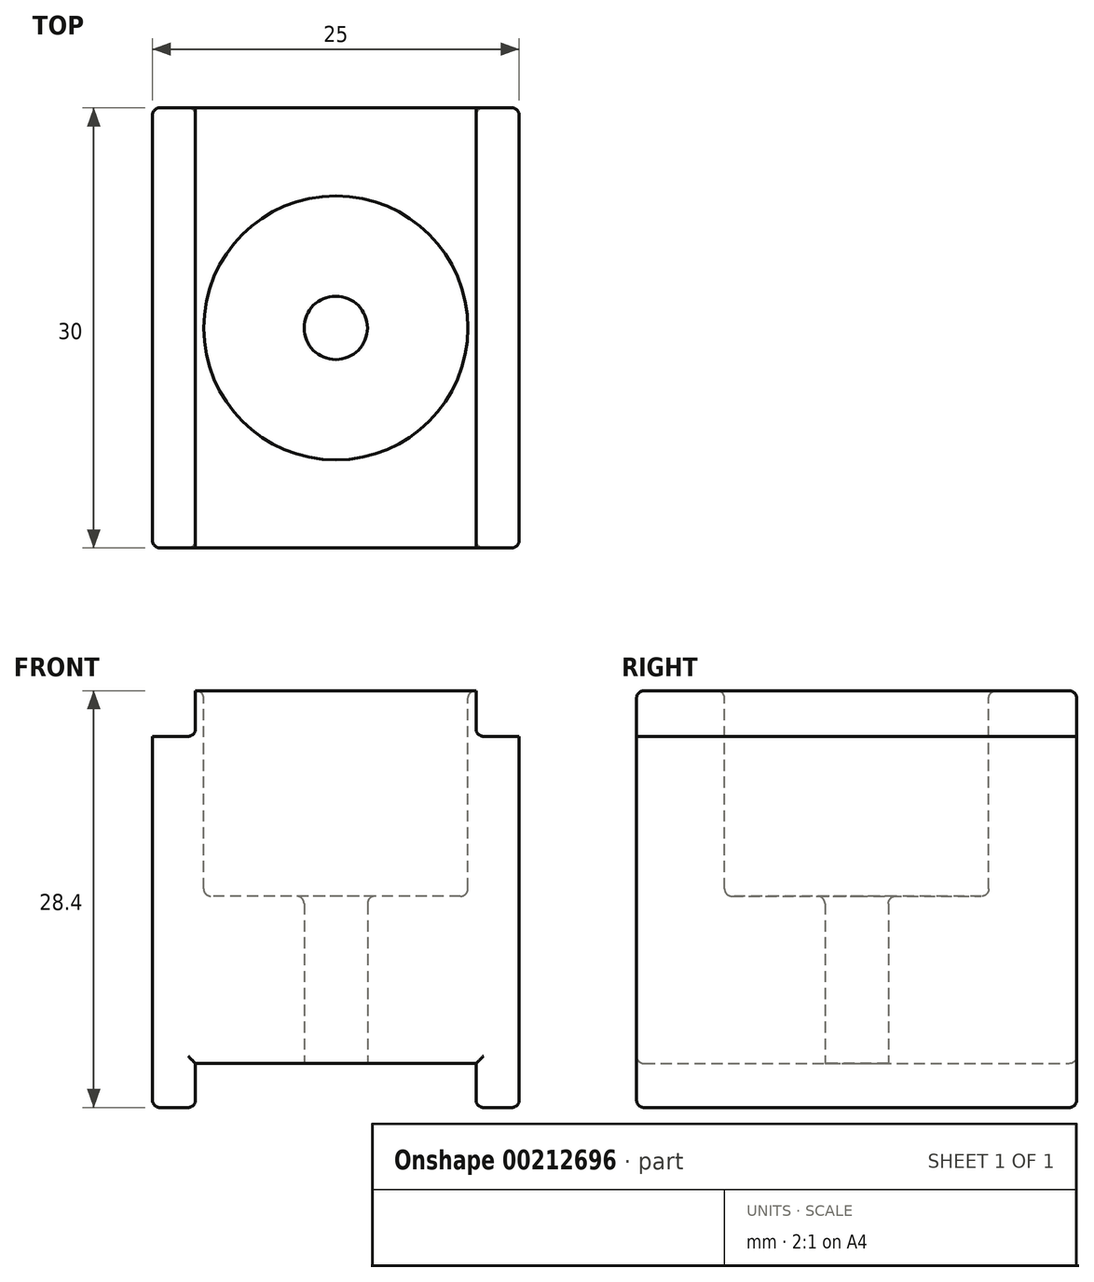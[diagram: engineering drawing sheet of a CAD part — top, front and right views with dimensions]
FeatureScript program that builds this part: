
annotation { "Feature Type Name" : "Feature", "Feature Type Description" : "" }
export const myFeature = defineFeature(function(context is Context, id is Id, definition is map)
    precondition{}
    {
        {
            var Q0;
            Q0=qCreatedBy(makeId("Top.planeOp"),FACE);
            var sketch = newSketch(context, id + "F0", { "sketchPlane" : qUnion([Q0])});
            skLineSegment(sketch, "E0.bottom", {"start": v(12.5, 15) * mm, "end": v(-12.5, 15) * mm});
            skLineSegment(sketch, "E0.top", {"start": v(12.5, -15) * mm, "end": v(-12.5, -15) * mm});
            skLineSegment(sketch, "E0.left", {"start": v(12.5, 15) * mm, "end": v(12.5, -15) * mm});
            skLineSegment(sketch, "E0.right", {"start": v(-12.5, 15) * mm, "end": v(-12.5, -15) * mm});
            skPoint(sketch, "E0.middle", {"position": v(0, 0) * mm});
            skPoint(sketch, "E1.end.orphan", {"position": v(-9.56, -15) * mm});
            skPoint(sketch, "E1.start.orphan", {"position": v(-9.56, 15) * mm});
            skPoint(sketch, "E2.MirrorCS.end.orphan", {"position": v(9.56, -15) * mm});
            skPoint(sketch, "E2.MirrorCS.start.orphan", {"position": v(9.56, 15) * mm});
            skSolve(sketch);
        }
        {
            var Q0;
            Q0=makeQuery(id+"F0.imprint","IMPRINT",FACE,{"disambiguationData":[TD([[makeQuery(id+"F0.imprint","IMPRINT",EDGE,{"derivedFrom":sQuery(id+"F0.wireOp",EDGE,"E0.bottom")}),1.0]])]});
            extrude(context, id + "F1", {"entities" : qUnion([Q0]), "endBound" : BoundingType.SYMMETRIC, "depth" : 25.4 * mm});
        }
        {
            var Q0;
            Q0=makeQuery(id+"F1.opExtrude","CAP_FACE",FACE,{"disambiguationData":[OSD([sQuery(id+"F0.wireOp",EDGE,"E0.bottom"),sQuery(id+"F0.wireOp",EDGE,"E0.top"),sQuery(id+"F0.wireOp",EDGE,"E0.left"),sQuery(id+"F0.wireOp",EDGE,"E0.right")])],"isStart":true});
            var sketch = newSketch(context, id + "F2", { "sketchPlane" : qUnion([Q0])});
            skLineSegment(sketch, "E3", {"start": v(-9.56, 15) * mm, "end": v(-9.56, -15) * mm});
            skLineSegment(sketch, "E4.MirrorCS", {"start": v(9.56, 15) * mm, "end": v(9.56, -15) * mm});
            skSolve(sketch);
        }
        {
            var Q0;
            {var subQ0=sQuery(id+"F2.wireOp",EDGE,"E3");Q0=makeQuery(id+"F2.imprint","IMPRINT",FACE,{"disambiguationData":[TD([[makeQuery(id+"F2.imprint","IMPRINT",EDGE,{"derivedFrom":subQ0}),-1.0]])]});}
            var Q1;
            {var subQ0=sQuery(id+"F2.wireOp",EDGE,"E4.MirrorCS");Q1=makeQuery(id+"F2.imprint","IMPRINT",FACE,{"disambiguationData":[TD([[makeQuery(id+"F2.imprint","IMPRINT",EDGE,{"derivedFrom":subQ0}),1.0]])]});}
            extrude(context, id + "F3", {"entities" : qUnion([Q0, Q1]), "operationType" : NewBodyOperationType.ADD, "depth" : 3 * mm});
        }
        {
            var Q0;
            Q0=makeQuery(id+"F1.opExtrude","CAP_FACE",FACE,{"disambiguationData":[OSD([sQuery(id+"F0.wireOp",EDGE,"E0.bottom"),sQuery(id+"F0.wireOp",EDGE,"E0.top"),sQuery(id+"F0.wireOp",EDGE,"E0.left"),sQuery(id+"F0.wireOp",EDGE,"E0.right")])],"isStart":false});
            var sketch = newSketch(context, id + "F4", { "sketchPlane" : qUnion([Q0])});
            skCircle(sketch, "E5", {"center": v(0, 0) * mm, "radius": 9 * mm});
            skLineSegment(sketch, "E6", {"start": v(-9.56, 15) * mm, "end": v(-9.56, -15) * mm});
            skLineSegment(sketch, "E7.MirrorCS", {"start": v(9.56, 15) * mm, "end": v(9.56, -15) * mm});
            skSolve(sketch);
        }
        {
            var Q0;
            Q0=makeQuery(id+"F4.imprint","IMPRINT",FACE,{"disambiguationData":[TD([[makeQuery(id+"F4.imprint","IMPRINT",EDGE,{"derivedFrom":sQuery(id+"F4.wireOp",EDGE,"E5")}),1.0]])]});
            extrude(context, id + "F5", {"entities" : qUnion([Q0]), "operationType" : NewBodyOperationType.REMOVE, "oppositeDirection" : true, "depth" : 14 * mm});
        }
        {
            var Q0;
            {var subQ0=sQuery(id+"F4.wireOp",EDGE,"E7.MirrorCS");Q0=makeQuery(id+"F4.imprint","IMPRINT",FACE,{"disambiguationData":[TD([[makeQuery(id+"F4.imprint","IMPRINT",EDGE,{"derivedFrom":subQ0}),1.0]])]});}
            var Q1;
            {var subQ0=sQuery(id+"F4.wireOp",EDGE,"E6");Q1=makeQuery(id+"F4.imprint","IMPRINT",FACE,{"disambiguationData":[TD([[makeQuery(id+"F4.imprint","IMPRINT",EDGE,{"derivedFrom":subQ0}),-1.0]])]});}
            extrude(context, id + "F6", {"entities" : qUnion([Q0, Q1]), "operationType" : NewBodyOperationType.REMOVE, "oppositeDirection" : true, "depth" : 3.1 * mm});
        }
        {
            var Q0;
            Q0=makeQuery(id+"F1.opExtrude","CAP_FACE",FACE,{"disambiguationData":[OSD([sQuery(id+"F0.wireOp",EDGE,"E0.bottom"),sQuery(id+"F0.wireOp",EDGE,"E0.top"),sQuery(id+"F0.wireOp",EDGE,"E0.left"),sQuery(id+"F0.wireOp",EDGE,"E0.right")])],"isStart":true});
            var sketch = newSketch(context, id + "F7", { "sketchPlane" : qUnion([Q0])});
            skCircle(sketch, "E8", {"center": v(0, 0) * mm, "radius": 2.16 * mm});
            skSolve(sketch);
        }
        {
            var Q0;
            Q0=makeQuery(id+"F7.imprint","IMPRINT",FACE,{"disambiguationData":[TD([[makeQuery(id+"F7.imprint","IMPRINT",EDGE,{"derivedFrom":sQuery(id+"F7.wireOp",EDGE,"E8")}),1.0]])]});
            extrude(context, id + "F8", {"entities" : qUnion([Q0]), "operationType" : NewBodyOperationType.REMOVE, "endBound" : BoundingType.THROUGH_ALL, "oppositeDirection" : true, "depth" : 25 * mm});
        }
        {
            var Q0;
            Q0=makeQuery(id+"F3.opExtrude","CAP_EDGE",EDGE,{"disambiguationData":[OSD([sQuery(id+"F0.wireOp",EDGE,"E0.right")])],"isStart":false});
            var Q1;
            Q1=makeQuery(id+"F3.opExtrude","CAP_EDGE",EDGE,{"disambiguationData":[OSD([sQuery(id+"F2.wireOp",EDGE,"E3")])],"isStart":false});
            var Q2;
            Q2=makeQuery(id+"F3.opExtrude","CAP_EDGE",EDGE,{"disambiguationData":[OSD([sQuery(id+"F2.wireOp",EDGE,"E4.MirrorCS")])],"isStart":false});
            var Q3;
            Q3=makeQuery(id+"F3.opExtrude","CAP_EDGE",EDGE,{"disambiguationData":[OSD([sQuery(id+"F0.wireOp",EDGE,"E0.left")])],"isStart":false});
            var Q4;
            Q4=makeQuery(id+"F1.opExtrude","CAP_EDGE",EDGE,{"disambiguationData":[OSD([sQuery(id+"F0.wireOp",EDGE,"E0.bottom")])],"isStart":true});
            var Q5;
            Q5=makeQuery(id+"F1.opExtrude","CAP_EDGE",EDGE,{"disambiguationData":[OSD([sQuery(id+"F0.wireOp",EDGE,"E0.top")])],"isStart":true});
            var Q6;
            {var subQ0=sQuery(id+"F0.wireOp",EDGE,"E0.left");var subQ1=sQuery(id+"F0.wireOp",EDGE,"E0.bottom");Q6=makeQuery(id+"F3.boolean.opBoolean","MERGE",EDGE,{"derivedFrom":[makeQuery(id+"F1.opExtrude","SWEPT_EDGE",EDGE,{"disambiguationData":[OSD([subQ1,subQ0])]}),makeQuery(id+"F3.opExtrude","SWEPT_EDGE",EDGE,{"disambiguationData":[OSD([subQ1,subQ0])]})]});}
            var Q7;
            {var subQ0=sQuery(id+"F0.wireOp",EDGE,"E0.left");var subQ1=sQuery(id+"F0.wireOp",EDGE,"E0.top");Q7=makeQuery(id+"F3.boolean.opBoolean","MERGE",EDGE,{"derivedFrom":[makeQuery(id+"F1.opExtrude","SWEPT_EDGE",EDGE,{"disambiguationData":[OSD([subQ1,subQ0])]}),makeQuery(id+"F3.opExtrude","SWEPT_EDGE",EDGE,{"disambiguationData":[OSD([subQ1,subQ0])]})]});}
            var Q8;
            {var subQ0=sQuery(id+"F0.wireOp",EDGE,"E0.right");var subQ1=sQuery(id+"F0.wireOp",EDGE,"E0.bottom");Q8=makeQuery(id+"F3.boolean.opBoolean","MERGE",EDGE,{"derivedFrom":[makeQuery(id+"F1.opExtrude","SWEPT_EDGE",EDGE,{"disambiguationData":[OSD([subQ1,subQ0])]}),makeQuery(id+"F3.opExtrude","SWEPT_EDGE",EDGE,{"disambiguationData":[OSD([subQ1,subQ0])]})]});}
            var Q9;
            Q9=makeQuery(id+"F1.opExtrude","CAP_EDGE",EDGE,{"disambiguationData":[OSD([sQuery(id+"F0.wireOp",EDGE,"E0.bottom")])],"isStart":false});
            var Q10;
            Q10=makeQuery(id+"F6.boolean.opBoolean","COPY",EDGE,{"derivedFrom":makeQuery(id+"F6.opExtrude","CAP_EDGE",EDGE,{"disambiguationData":[OSD([sQuery(id+"F0.wireOp",EDGE,"E0.left")])],"isStart":false})});
            var Q11;
            Q11=makeQuery(id+"F6.boolean.opBoolean","COPY",EDGE,{"derivedFrom":makeQuery(id+"F6.opExtrude","CAP_EDGE",EDGE,{"disambiguationData":[OSD([sQuery(id+"F4.wireOp",EDGE,"E7.MirrorCS")])],"isStart":true})});
            var Q12;
            Q12=makeQuery(id+"F6.boolean.opBoolean","COPY",EDGE,{"derivedFrom":makeQuery(id+"F6.opExtrude","CAP_EDGE",EDGE,{"disambiguationData":[OSD([sQuery(id+"F4.wireOp",EDGE,"E6")])],"isStart":true})});
            var Q13;
            Q13=makeQuery(id+"F6.boolean.opBoolean","COPY",EDGE,{"derivedFrom":makeQuery(id+"F6.opExtrude","CAP_EDGE",EDGE,{"disambiguationData":[OSD([sQuery(id+"F0.wireOp",EDGE,"E0.right")])],"isStart":false})});
            var Q14;
            Q14=makeQuery(id+"F1.opExtrude","CAP_EDGE",EDGE,{"disambiguationData":[OSD([sQuery(id+"F0.wireOp",EDGE,"E0.top")])],"isStart":false});
            var Q15;
            Q15=makeQuery(id+"F6.boolean.opBoolean","COPY",EDGE,{"derivedFrom":makeQuery(id+"F6.opExtrude","CAP_EDGE",EDGE,{"disambiguationData":[OSD([sQuery(id+"F4.wireOp",EDGE,"E7.MirrorCS")])],"isStart":false})});
            var Q16;
            Q16=makeQuery(id+"F6.boolean.opBoolean","COPY",EDGE,{"derivedFrom":makeQuery(id+"F6.opExtrude","CAP_EDGE",EDGE,{"disambiguationData":[OSD([sQuery(id+"F4.wireOp",EDGE,"E6")])],"isStart":false})});
            var Q17;
            Q17=makeQuery(id+"F3.opExtrude","CAP_EDGE",EDGE,{"disambiguationData":[OSD([sQuery(id+"F2.wireOp",EDGE,"E4.MirrorCS")])],"isStart":true});
            var Q18;
            Q18=makeQuery(id+"F3.opExtrude","CAP_EDGE",EDGE,{"disambiguationData":[OSD([sQuery(id+"F2.wireOp",EDGE,"E3")])],"isStart":true});
            fillet(context, id + "F9", {"entities" : qUnion([Q0, Q1, Q2, Q3, Q4, Q5, Q6, Q7, Q8, Q9, Q10, Q11, Q12, Q13, Q14, Q15, Q16, Q17, Q18]), "radius" : .5 * mm, "tangentPropagation" : true, "allowEdgeOverflow" : false});
        }
        {
            var Q0;
            Q0=makeQuery(id+"F6.boolean.opBoolean","COPY",EDGE,{"derivedFrom":makeQuery(id+"F6.opExtrude","SWEPT_EDGE",EDGE,{"disambiguationData":[OSD([sQuery(id+"F0.wireOp",EDGE,"E0.bottom"),sQuery(id+"F4.wireOp",EDGE,"E6")])]})});
            var Q1;
            Q1=makeQuery(id+"F6.boolean.opBoolean","COPY",EDGE,{"derivedFrom":makeQuery(id+"F6.opExtrude","SWEPT_EDGE",EDGE,{"disambiguationData":[OSD([sQuery(id+"F0.wireOp",EDGE,"E0.bottom"),sQuery(id+"F4.wireOp",EDGE,"E7.MirrorCS")])]})});
            var Q2;
            {var subQ0=sQuery(id+"F0.wireOp",EDGE,"E0.bottom");var subQ1=makeQuery(id+"F1.opExtrude","CAP_EDGE",EDGE,{"disambiguationData":[OSD([subQ0])],"isStart":true});Q2=makeQuery(id+"F3.opExtrude","CAP_EDGE",EDGE,{"disambiguationData":[OSD([subQ0]),TDD([makeQuery(id+"F2.imprint","IMPRINT",EDGE,{"disambiguationData":[TD([[makeQuery(id+"F2.imprint","INTERSECT",VERTEX,{"derivedFrom":[subQ1,makeQuery(id+"F1.opExtrude","CAP_EDGE",EDGE,{"disambiguationData":[OSD([sQuery(id+"F0.wireOp",EDGE,"E0.left")])],"isStart":true})]}),-1.0]])],"derivedFrom":subQ1})])],"isStart":false});}
            var Q3;
            {var subQ0=sQuery(id+"F0.wireOp",EDGE,"E0.bottom");var subQ1=makeQuery(id+"F1.opExtrude","CAP_EDGE",EDGE,{"disambiguationData":[OSD([subQ0])],"isStart":true});Q3=makeQuery(id+"F3.opExtrude","CAP_EDGE",EDGE,{"disambiguationData":[OSD([subQ0]),TDD([makeQuery(id+"F2.imprint","IMPRINT",EDGE,{"disambiguationData":[TD([[makeQuery(id+"F2.imprint","INTERSECT",VERTEX,{"derivedFrom":[subQ1,makeQuery(id+"F1.opExtrude","CAP_EDGE",EDGE,{"disambiguationData":[OSD([sQuery(id+"F0.wireOp",EDGE,"E0.right")])],"isStart":true})]}),1.0]])],"derivedFrom":subQ1})])],"isStart":false});}
            var Q4;
            {var subQ0=sQuery(id+"F0.wireOp",EDGE,"E0.top");var subQ1=makeQuery(id+"F1.opExtrude","CAP_EDGE",EDGE,{"disambiguationData":[OSD([subQ0])],"isStart":true});Q4=makeQuery(id+"F3.opExtrude","CAP_EDGE",EDGE,{"disambiguationData":[OSD([subQ0]),TDD([makeQuery(id+"F2.imprint","IMPRINT",EDGE,{"disambiguationData":[TD([[makeQuery(id+"F2.imprint","INTERSECT",VERTEX,{"derivedFrom":[subQ1,makeQuery(id+"F1.opExtrude","CAP_EDGE",EDGE,{"disambiguationData":[OSD([sQuery(id+"F0.wireOp",EDGE,"E0.right")])],"isStart":true})]}),1.0]])],"derivedFrom":subQ1})])],"isStart":false});}
            var Q5;
            {var subQ0=sQuery(id+"F0.wireOp",EDGE,"E0.top");var subQ1=makeQuery(id+"F1.opExtrude","CAP_EDGE",EDGE,{"disambiguationData":[OSD([subQ0])],"isStart":true});Q5=makeQuery(id+"F3.opExtrude","CAP_EDGE",EDGE,{"disambiguationData":[OSD([subQ0]),TDD([makeQuery(id+"F2.imprint","IMPRINT",EDGE,{"disambiguationData":[TD([[makeQuery(id+"F2.imprint","INTERSECT",VERTEX,{"derivedFrom":[subQ1,makeQuery(id+"F1.opExtrude","CAP_EDGE",EDGE,{"disambiguationData":[OSD([sQuery(id+"F0.wireOp",EDGE,"E0.left")])],"isStart":true})]}),-1.0]])],"derivedFrom":subQ1})])],"isStart":false});}
            var Q6;
            {var subQ0=sQuery(id+"F0.wireOp",EDGE,"E0.top");var subQ1=makeQuery(id+"F1.opExtrude","CAP_EDGE",EDGE,{"disambiguationData":[OSD([subQ0])],"isStart":false});Q6=makeQuery(id+"F6.boolean.opBoolean","COPY",EDGE,{"derivedFrom":makeQuery(id+"F6.opExtrude","CAP_EDGE",EDGE,{"disambiguationData":[OSD([subQ0]),TDD([makeQuery(id+"F4.imprint","IMPRINT",EDGE,{"disambiguationData":[TD([[makeQuery(id+"F4.imprint","INTERSECT",VERTEX,{"derivedFrom":[subQ1,makeQuery(id+"F1.opExtrude","CAP_EDGE",EDGE,{"disambiguationData":[OSD([sQuery(id+"F0.wireOp",EDGE,"E0.left")])],"isStart":false})]}),-1.0]])],"derivedFrom":subQ1})])],"isStart":false})});}
            var Q7;
            Q7=makeQuery(id+"F5.boolean.opBoolean","COPY",EDGE,{"derivedFrom":makeQuery(id+"F5.opExtrude","CAP_EDGE",EDGE,{"disambiguationData":[OSD([sQuery(id+"F4.wireOp",EDGE,"E5")])],"isStart":true})});
            var Q8;
            Q8=makeQuery(id+"F8.boolean.opBoolean","INTERSECT",EDGE,{"derivedFrom":[makeQuery(id+"F5.boolean.opBoolean","COPY",FACE,{"derivedFrom":makeQuery(id+"F5.opExtrude","CAP_FACE",FACE,{"disambiguationData":[OSD([sQuery(id+"F4.wireOp",EDGE,"E5")])],"isStart":false})}),makeQuery(id+"F8.opExtrude","SWEPT_FACE",FACE,{"disambiguationData":[OSD([sQuery(id+"F7.wireOp",EDGE,"E8")])]})]});
            var Q9;
            Q9=makeQuery(id+"F5.boolean.opBoolean","COPY",FACE,{"derivedFrom":makeQuery(id+"F5.opExtrude","SWEPT_FACE",FACE,{"disambiguationData":[OSD([sQuery(id+"F4.wireOp",EDGE,"E5")])]})});
            var Q10;
            Q10=makeQuery(id+"F8.boolean.opBoolean","COPY",EDGE,{"derivedFrom":makeQuery(id+"F8.opExtrude","CAP_EDGE",EDGE,{"disambiguationData":[OSD([sQuery(id+"F7.wireOp",EDGE,"E8")])],"isStart":true})});
            fillet(context, id + "F10", {"entities" : qUnion([Q0, Q1, Q2, Q3, Q4, Q5, Q6, Q7, Q8, Q9, Q10]), "radius" : .5 * mm, "tangentPropagation" : true, "allowEdgeOverflow" : false});
        }
    });
